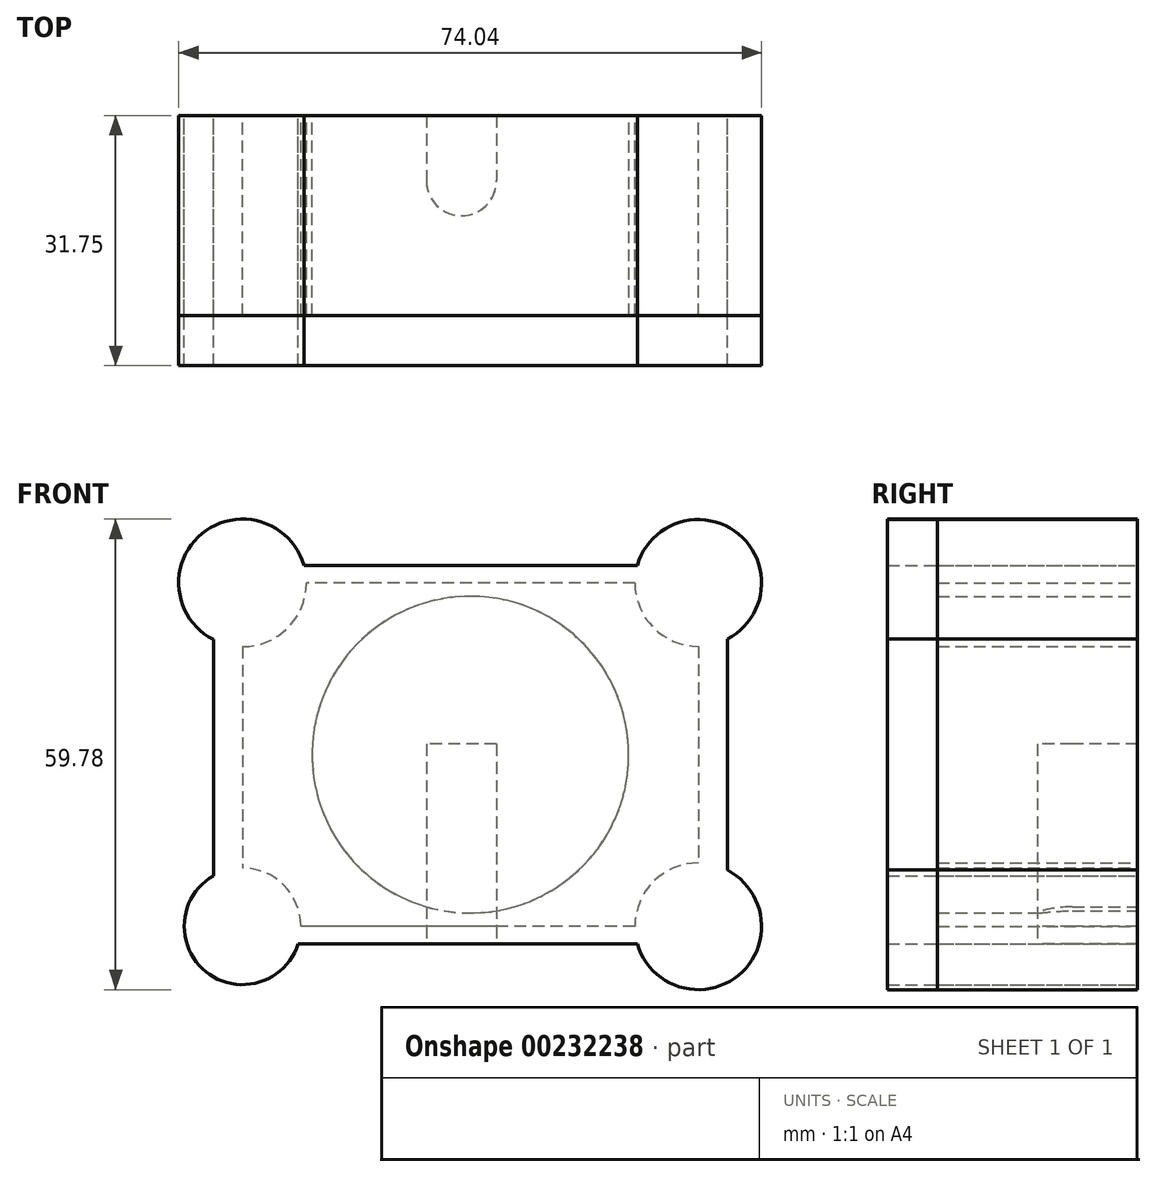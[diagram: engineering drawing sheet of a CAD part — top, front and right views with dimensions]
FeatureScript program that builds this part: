
annotation { "Feature Type Name" : "Feature", "Feature Type Description" : "" }
export const myFeature = defineFeature(function(context is Context, id is Id, definition is map)
    precondition{}
    {
        {
            var Q0;
            Q0=qCreatedBy(makeId("Front.planeOp"),FACE);
            var sketch = newSketch(context, id + "F0", { "sketchPlane" : qUnion([Q0])});
            skLineSegment(sketch, "E0.bottom", {"start": v(20.9, 21.82) * mm, "end": v(-20.84, 21.82) * mm});
            skLineSegment(sketch, "E0.top", {"start": v(20.9, -21.82) * mm, "end": v(-21.54, -21.82) * mm});
            skLineSegment(sketch, "E0.left", {"start": v(28.94, 13.77) * mm, "end": v(28.94, -13.77) * mm});
            skLineSegment(sketch, "E0.right", {"start": v(-28.94, 13.71) * mm, "end": v(-28.94, -14.4) * mm});
            skPoint(sketch, "E0.middle", {"position": v(0, 0) * mm});
            skCircle(sketch, "E1", {"center": v(0, 0) * mm, "radius": 20.12 * mm});
            skCircle(sketch, "E2", {"center": v(-28.94, 21.82) * mm, "radius": 8.1 * mm});
            skCircle(sketch, "E3", {"center": v(28.94, 21.82) * mm, "radius": 8.04 * mm});
            skCircle(sketch, "E4", {"center": v(-28.94, -21.82) * mm, "radius": 7.4 * mm});
            skCircle(sketch, "E5", {"center": v(28.94, -21.82) * mm, "radius": 8.04 * mm});
            skLineSegment(sketch, "E6.bottom", {"start": v(21.22, -24.05) * mm, "end": v(-21.88, -24.05) * mm});
            skLineSegment(sketch, "E6.top", {"start": v(21.22, 24.05) * mm, "end": v(-21.15, 24.05) * mm});
            skLineSegment(sketch, "E6.left", {"start": v(32.65, -24.05) * mm, "end": v(32.65, 14.67) * mm});
            skLineSegment(sketch, "E6.right", {"start": v(-32.65, -15.4) * mm, "end": v(-32.65, 14.6) * mm});
            skPoint(sketch, "E7.orphan", {"position": v(-32.65, 24.05) * mm});
            skPoint(sketch, "E8.orphan", {"position": v(-32.65, -24.05) * mm});
            skPoint(sketch, "E9.orphan", {"position": v(32.65, 24.05) * mm});
            skSolve(sketch);
        }
        {
            var Q0;
            {var subQ0=sQuery(id+"F0.wireOp",EDGE,"E2");var subQ1=makeQuery(id+"F0.imprint","INTERSECT",VERTEX,{"derivedFrom":[sQuery(id+"F0.wireOp",EDGE,"E0.bottom"),subQ0]});Q0=makeQuery(id+"F0.imprint","IMPRINT",FACE,{"disambiguationData":[TD([[makeQuery(id+"F0.imprint","IMPRINT",EDGE,{"disambiguationData":[TD([[subQ1,-1.0]])],"derivedFrom":subQ0}),1.0]])]});}
            var Q1;
            {var subQ0=sQuery(id+"F0.wireOp",EDGE,"E4");var subQ1=makeQuery(id+"F0.imprint","INTERSECT",VERTEX,{"derivedFrom":[sQuery(id+"F0.wireOp",EDGE,"E0.top"),subQ0]});Q1=makeQuery(id+"F0.imprint","IMPRINT",FACE,{"disambiguationData":[TD([[makeQuery(id+"F0.imprint","IMPRINT",EDGE,{"disambiguationData":[TD([[subQ1,-1.0]])],"derivedFrom":subQ0}),1.0]])]});}
            var Q2;
            {var subQ0=sQuery(id+"F0.wireOp",EDGE,"E3");var subQ1=makeQuery(id+"F0.imprint","INTERSECT",VERTEX,{"derivedFrom":[sQuery(id+"F0.wireOp",EDGE,"E0.bottom"),subQ0]});Q2=makeQuery(id+"F0.imprint","IMPRINT",FACE,{"disambiguationData":[TD([[makeQuery(id+"F0.imprint","IMPRINT",EDGE,{"disambiguationData":[TD([[subQ1,1.0]])],"derivedFrom":subQ0}),1.0]])]});}
            var Q3;
            {var subQ0=sQuery(id+"F0.wireOp",EDGE,"E5");var subQ1=makeQuery(id+"F0.imprint","INTERSECT",VERTEX,{"derivedFrom":[sQuery(id+"F0.wireOp",EDGE,"E0.left"),subQ0]});Q3=makeQuery(id+"F0.imprint","IMPRINT",FACE,{"disambiguationData":[TD([[makeQuery(id+"F0.imprint","IMPRINT",EDGE,{"disambiguationData":[TD([[subQ1,1.0]])],"derivedFrom":subQ0}),1.0]])]});}
            var Q4;
            {var subQ0=sQuery(id+"F0.wireOp",EDGE,"E0.bottom");Q4=makeQuery(id+"F0.imprint","IMPRINT",FACE,{"disambiguationData":[TD([[makeQuery(id+"F0.imprint","IMPRINT",EDGE,{"derivedFrom":subQ0}),-1.0]])]});}
            var Q5;
            {var subQ0=sQuery(id+"F0.wireOp",EDGE,"E0.right");Q5=makeQuery(id+"F0.imprint","IMPRINT",FACE,{"disambiguationData":[TD([[makeQuery(id+"F0.imprint","IMPRINT",EDGE,{"derivedFrom":subQ0}),-1.0]])]});}
            var Q6;
            {var subQ0=sQuery(id+"F0.wireOp",EDGE,"E0.left");Q6=makeQuery(id+"F0.imprint","IMPRINT",FACE,{"disambiguationData":[TD([[makeQuery(id+"F0.imprint","IMPRINT",EDGE,{"derivedFrom":subQ0}),1.0]])]});}
            var Q7;
            {var subQ0=sQuery(id+"F0.wireOp",EDGE,"E0.top");Q7=makeQuery(id+"F0.imprint","IMPRINT",FACE,{"disambiguationData":[TD([[makeQuery(id+"F0.imprint","IMPRINT",EDGE,{"derivedFrom":subQ0}),1.0]])]});}
            var Q8;
            Q8=makeQuery(id+"F0.imprint","IMPRINT",FACE,{"disambiguationData":[TD([[makeQuery(id+"F0.imprint","IMPRINT",EDGE,{"derivedFrom":sQuery(id+"F0.wireOp",EDGE,"E1")}),1.0]])]});
            var Q9;
            {var subQ2=sQuery(id+"F0.wireOp",EDGE,"E0.bottom");Q9=makeQuery(id+"F0.imprint","IMPRINT",FACE,{"disambiguationData":[TD([[makeQuery(id+"F0.imprint","IMPRINT",EDGE,{"derivedFrom":subQ2}),1.0]])]});}
            extrude(context, id + "F1", {"entities" : qUnion([Q0, Q1, Q2, Q3, Q4, Q5, Q6, Q7, Q8, Q9]), "depth" : 31.75 * mm});
        }
        {
            var Q0;
            Q0 = qSketchRegion(id + "F0", true);
            var Q1;
            Q1=makeQuery(id+"F0.imprint","IMPRINT",FACE,{"disambiguationData":[TD([[makeQuery(id+"F0.imprint","IMPRINT",EDGE,{"derivedFrom":sQuery(id+"F0.wireOp",EDGE,"E1")}),1.0]])]});
            extrude(context, id + "F2", {"entities" : qUnion([Q0, Q1]), "depth" : 25.4 * mm});
        }
        {
            var Q0;
            Q0=makeQuery(id+"F2.opExtrude","SWEPT_FACE",FACE,{"disambiguationData":[OSD([sQuery(id+"F0.wireOp",EDGE,"E6.bottom")])]});
            var sketch = newSketch(context, id + "F3", { "sketchPlane" : qUnion([Q0])});
            skLineSegment(sketch, "E10.bottom", {"start": v(-5.58, 0) * mm, "end": v(3.3, 0) * mm});
            skLineSegment(sketch, "E10.left", {"start": v(-5.58, 0) * mm, "end": v(-5.58, 8.27) * mm});
            skLineSegment(sketch, "E10.right", {"start": v(3.3, 0) * mm, "end": v(3.3, 8.27) * mm});
            skArc(sketch, "E11", {"start": v(3.3, 8.27) * mm, "mid": v(-1.14, 12.71) * mm, "end": v(-5.58, 8.27) * mm});
            skSolve(sketch);
        }
        {
            var Q0;
            Q0=makeQuery(id+"F3.imprint","IMPRINT",FACE,{"disambiguationData":[TD([[makeQuery(id+"F3.imprint","IMPRINT",EDGE,{"derivedFrom":sQuery(id+"F3.wireOp",EDGE,"E10.bottom")}),-1.0]])]});
            extrude(context, id + "F4", {"entities" : qUnion([Q0]), "operationType" : NewBodyOperationType.REMOVE, "oppositeDirection" : true, "depth" : 25.4 * mm});
        }
    });
